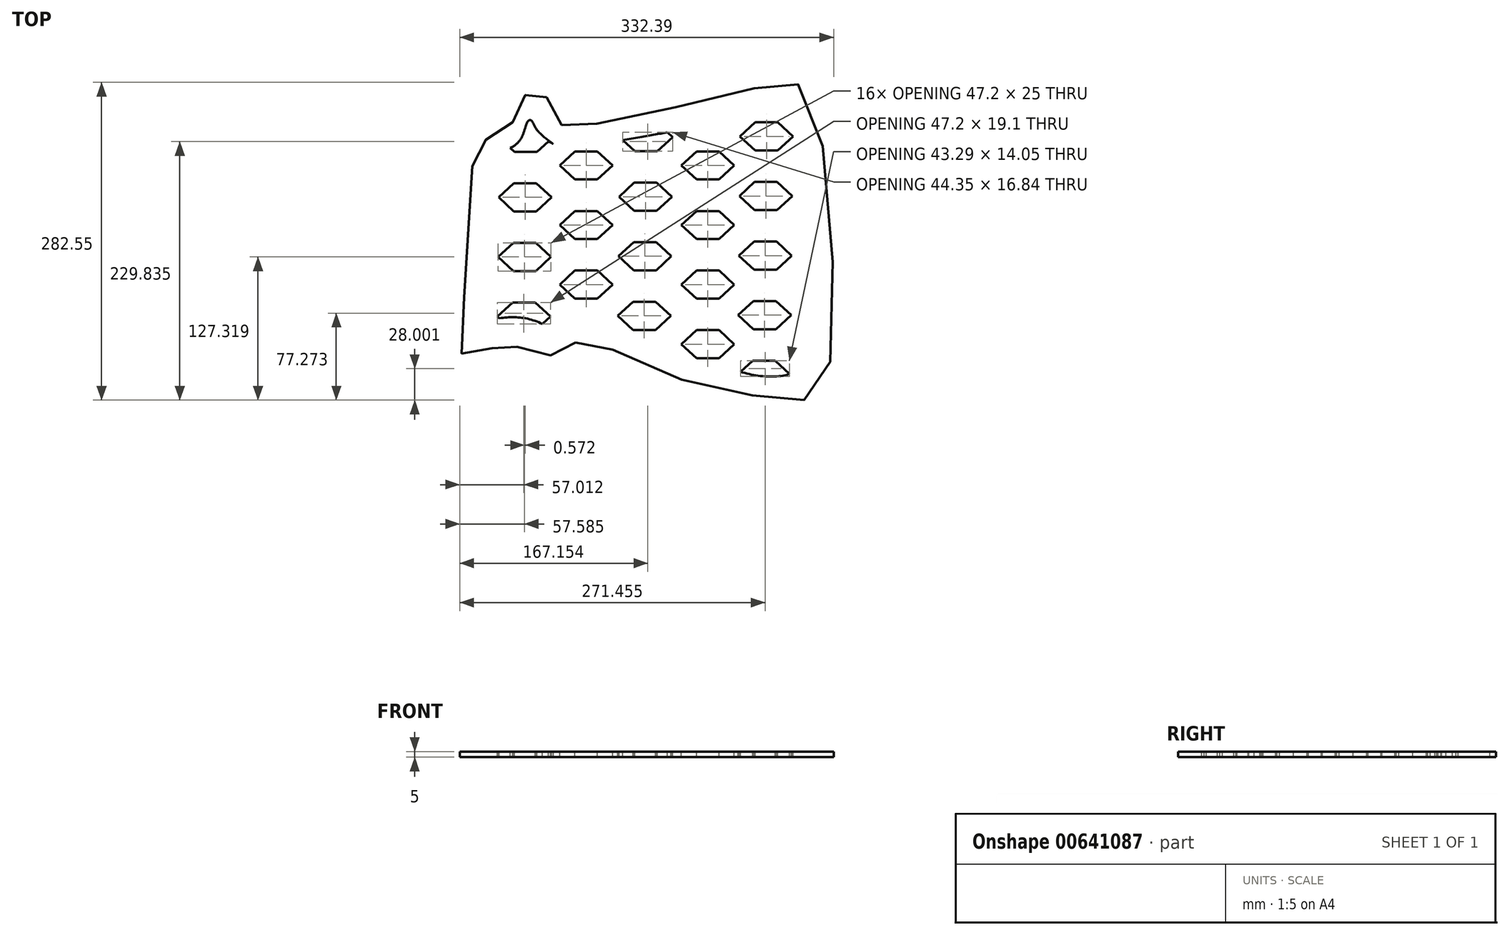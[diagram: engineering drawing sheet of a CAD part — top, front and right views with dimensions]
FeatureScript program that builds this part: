
annotation { "Feature Type Name" : "Feature", "Feature Type Description" : "" }
export const myFeature = defineFeature(function(context is Context, id is Id, definition is map)
    precondition{}
    {
        {
            var Q0;
            Q0=qCreatedBy(makeId("Top.planeOp"),FACE);
            var sketch = newSketch(context, id + "F0", { "sketchPlane" : qUnion([Q0])});
            skFitSpline(sketch, "E0", {"points": [v(-94.07, -91.9) * mm, v(-73.28, -91.9) * mm, v(-51.22, -104.21) * mm, v(37.87, -135.18) * mm, v(78.6, -140.27) * mm, v(113.8, -141.97) * mm, v(129.5, -122.03) * mm, v(133.1, 8.11) * mm, v(111.47, 130.93) * mm, v(94.35, 139.49) * mm, v(62.95, 133.78) * mm, v(-26.95, 112.38) * mm, v(-91.16, 100.96) * mm, v(-103.99, 100.98) * mm, v(-106.66, 101.88) * mm, v(-111.48, 110.97) * mm, v(-119.2, 125.34) * mm, v(-130.98, 133.72) * mm, v(-136.33, 132.65) * mm, v(-140.08, 124.45) * mm, v(-144.54, 111.78) * mm, v(-151.14, 102.68) * mm, v(-161.84, 93.4) * mm, v(-175.4, 88.06) * mm, v(-183.06, 84.5) * mm, v(-185.2, 75.21) * mm, v(-196.64, -95.2) * mm, v(-196.85, -99.64) * mm, v(-194.63, -102.29) * mm, v(-190.38, -103.77) * mm, v(-170.02, -97.51) * mm, v(-163.87, -94.97) * mm, v(-157.5, -91.79) * mm, v(-139.47, -99) * mm, v(-122.77, -103.85) * mm, v(-112.2, -101.6) * mm, v(-101.44, -94.98) * mm, v(-94.07, -91.9) * mm]});
            skSolve(sketch);
        }
        {
            var Q0;
            Q0 = qSketchRegion(id + "F0", true);
            extrude(context, id + "F1", {"entities" : qUnion([Q0]), "depth" : 5 * mm, "offsetDistance" : 25.4 * mm});
        }
        {
            var Q0;
            Q0=makeQuery(id+"F1.opExtrude","CAP_FACE",FACE,{"disambiguationData":[OSD([sQuery(id+"F0.wireOp",EDGE,"E0")])],"isStart":false});
            var sketch = newSketch(context, id + "F2", { "sketchPlane" : qUnion([Q0])});
            skLineSegment(sketch, "E1.bottom", {"start": v(65.65, 103.96) * mm, "end": v(85.65, 103.96) * mm});
            skLineSegment(sketch, "E1.top", {"start": v(65.65, 78.96) * mm, "end": v(85.65, 78.96) * mm});
            skLineSegment(sketch, "E2", {"start": v(65.65, 103.96) * mm, "end": v(52.05, 91.46) * mm});
            skPoint(sketch, "E2.endSnap0", {"position": v(65.65, 91.46) * mm});
            skLineSegment(sketch, "E3", {"start": v(52.05, 91.46) * mm, "end": v(65.65, 78.96) * mm});
            skLineSegment(sketch, "E4.MirrorCS", {"start": v(85.65, 103.96) * mm, "end": v(99.24, 91.46) * mm});
            skLineSegment(sketch, "E5.MirrorCS", {"start": v(99.24, 91.46) * mm, "end": v(85.65, 78.96) * mm});
            skLineSegment(sketch, "E6.0.1.0", {"start": v(-52.1, 88.23) * mm, "end": v(-41.35, 78.35) * mm});
            skLineSegment(sketch, "E6.0.1.1", {"start": v(-41.35, 103.35) * mm, "end": v(-54.95, 90.85) * mm});
            skLineSegment(sketch, "E6.0.1.2", {"start": v(-41.35, 103.35) * mm, "end": v(-21.35, 103.35) * mm});
            skLineSegment(sketch, "E6.0.1.3", {"start": v(-12.48, 95.2) * mm, "end": v(-7.75, 90.85) * mm});
            skLineSegment(sketch, "E6.0.1.4", {"start": v(-7.75, 90.85) * mm, "end": v(-21.35, 78.35) * mm});
            skLineSegment(sketch, "E6.0.1.5", {"start": v(-41.35, 78.35) * mm, "end": v(-21.35, 78.35) * mm});
            skLineSegment(sketch, "E6.1.0.0", {"start": v(51.47, 38.46) * mm, "end": v(65.07, 25.96) * mm});
            skLineSegment(sketch, "E6.1.0.1", {"start": v(65.07, 50.96) * mm, "end": v(51.47, 38.46) * mm});
            skLineSegment(sketch, "E6.1.0.2", {"start": v(65.07, 50.96) * mm, "end": v(85.07, 50.96) * mm});
            skLineSegment(sketch, "E6.1.0.3", {"start": v(85.07, 50.96) * mm, "end": v(98.67, 38.46) * mm});
            skLineSegment(sketch, "E6.1.0.4", {"start": v(98.67, 38.46) * mm, "end": v(85.07, 25.96) * mm});
            skLineSegment(sketch, "E6.1.0.5", {"start": v(65.07, 25.96) * mm, "end": v(85.07, 25.96) * mm});
            skLineSegment(sketch, "E6.1.1.0", {"start": v(-55.52, 37.86) * mm, "end": v(-41.92, 25.36) * mm});
            skLineSegment(sketch, "E6.1.1.1", {"start": v(-41.92, 50.36) * mm, "end": v(-55.52, 37.86) * mm});
            skLineSegment(sketch, "E6.1.1.2", {"start": v(-41.92, 50.36) * mm, "end": v(-21.92, 50.36) * mm});
            skLineSegment(sketch, "E6.1.1.3", {"start": v(-21.92, 50.36) * mm, "end": v(-8.33, 37.86) * mm});
            skLineSegment(sketch, "E6.1.1.4", {"start": v(-8.33, 37.86) * mm, "end": v(-21.92, 25.36) * mm});
            skLineSegment(sketch, "E6.1.1.5", {"start": v(-41.92, 25.36) * mm, "end": v(-21.92, 25.36) * mm});
            skLineSegment(sketch, "E6.2.0.0", {"start": v(50.9, -14.54) * mm, "end": v(64.5, -27.04) * mm});
            skLineSegment(sketch, "E6.2.0.1", {"start": v(64.5, -2.04) * mm, "end": v(50.9, -14.54) * mm});
            skLineSegment(sketch, "E6.2.0.2", {"start": v(64.5, -2.04) * mm, "end": v(84.5, -2.04) * mm});
            skLineSegment(sketch, "E6.2.0.3", {"start": v(84.5, -2.04) * mm, "end": v(98.1, -14.54) * mm});
            skLineSegment(sketch, "E6.2.0.4", {"start": v(98.1, -14.54) * mm, "end": v(84.5, -27.04) * mm});
            skLineSegment(sketch, "E6.2.0.5", {"start": v(64.5, -27.04) * mm, "end": v(84.5, -27.04) * mm});
            skLineSegment(sketch, "E6.2.1.0", {"start": v(-56.1, -15.14) * mm, "end": v(-42.5, -27.64) * mm});
            skLineSegment(sketch, "E6.2.1.1", {"start": v(-42.5, -2.64) * mm, "end": v(-56.1, -15.14) * mm});
            skLineSegment(sketch, "E6.2.1.2", {"start": v(-42.5, -2.64) * mm, "end": v(-22.5, -2.64) * mm});
            skLineSegment(sketch, "E6.2.1.3", {"start": v(-22.5, -2.64) * mm, "end": v(-8.9, -15.14) * mm});
            skLineSegment(sketch, "E6.2.1.4", {"start": v(-8.9, -15.14) * mm, "end": v(-22.5, -27.64) * mm});
            skLineSegment(sketch, "E6.2.1.5", {"start": v(-42.5, -27.64) * mm, "end": v(-22.5, -27.64) * mm});
            skLineSegment(sketch, "E6.direction1", {"start": v(52.05, 91.46) * mm, "end": v(51.47, 38.46) * mm, "construction": true});
            skLineSegment(sketch, "E6.direction2", {"start": v(52.05, 91.46) * mm, "end": v(-54.95, 90.85) * mm, "construction": true});
            skLineSegment(sketch, "E7.0.0.2", {"start": v(-152.06, 81.16) * mm, "end": v(-148.35, 77.75) * mm});
            skLineSegment(sketch, "E7.3.0.2", {"start": v(-148.35, 102.75) * mm, "end": v(-161.95, 90.25) * mm});
            skLineSegment(sketch, "E7.6.0.2", {"start": v(-148.35, 102.75) * mm, "end": v(-128.35, 102.75) * mm});
            skLineSegment(sketch, "E7.9.0.2", {"start": v(-128.35, 102.75) * mm, "end": v(-114.75, 90.25) * mm});
            skLineSegment(sketch, "E7.12.0.2", {"start": v(-117.71, 87.53) * mm, "end": v(-128.35, 77.75) * mm});
            skLineSegment(sketch, "E7.15.0.2", {"start": v(-148.35, 77.75) * mm, "end": v(-128.35, 77.75) * mm});
            skLineSegment(sketch, "E7.0.1.2", {"start": v(-162.52, 37.26) * mm, "end": v(-148.92, 24.76) * mm});
            skLineSegment(sketch, "E7.3.1.2", {"start": v(-148.92, 49.76) * mm, "end": v(-162.52, 37.26) * mm});
            skLineSegment(sketch, "E7.6.1.2", {"start": v(-148.92, 49.76) * mm, "end": v(-128.92, 49.76) * mm});
            skLineSegment(sketch, "E7.9.1.2", {"start": v(-128.92, 49.76) * mm, "end": v(-115.32, 37.26) * mm});
            skLineSegment(sketch, "E7.12.1.2", {"start": v(-115.32, 37.26) * mm, "end": v(-128.92, 24.76) * mm});
            skLineSegment(sketch, "E7.15.1.2", {"start": v(-148.92, 24.76) * mm, "end": v(-128.92, 24.76) * mm});
            skLineSegment(sketch, "E7.0.2.2", {"start": v(-163.1, -15.74) * mm, "end": v(-149.5, -28.24) * mm});
            skLineSegment(sketch, "E7.3.2.2", {"start": v(-149.5, -3.24) * mm, "end": v(-163.1, -15.74) * mm});
            skLineSegment(sketch, "E7.6.2.2", {"start": v(-149.5, -3.24) * mm, "end": v(-129.5, -3.24) * mm});
            skLineSegment(sketch, "E7.9.2.2", {"start": v(-129.5, -3.24) * mm, "end": v(-115.9, -15.74) * mm});
            skLineSegment(sketch, "E7.12.2.2", {"start": v(-115.9, -15.74) * mm, "end": v(-129.5, -28.24) * mm});
            skLineSegment(sketch, "E7.15.2.2", {"start": v(-149.5, -28.24) * mm, "end": v(-129.5, -28.24) * mm});
            skLineSegment(sketch, "E8.0.3.0", {"start": v(50.33, -67.54) * mm, "end": v(63.93, -80.04) * mm});
            skLineSegment(sketch, "E8.3.3.0", {"start": v(63.93, -55.04) * mm, "end": v(50.33, -67.54) * mm});
            skLineSegment(sketch, "E8.6.3.0", {"start": v(63.93, -55.04) * mm, "end": v(83.93, -55.04) * mm});
            skLineSegment(sketch, "E8.9.3.0", {"start": v(83.93, -55.04) * mm, "end": v(97.53, -67.54) * mm});
            skLineSegment(sketch, "E8.12.3.0", {"start": v(97.53, -67.54) * mm, "end": v(83.93, -80.04) * mm});
            skLineSegment(sketch, "E8.15.3.0", {"start": v(63.93, -80.04) * mm, "end": v(83.93, -80.04) * mm});
            skLineSegment(sketch, "E8.0.3.1", {"start": v(-56.67, -68.14) * mm, "end": v(-43.07, -80.64) * mm});
            skLineSegment(sketch, "E8.3.3.1", {"start": v(-43.07, -55.64) * mm, "end": v(-56.67, -68.14) * mm});
            skLineSegment(sketch, "E8.6.3.1", {"start": v(-43.07, -55.64) * mm, "end": v(-23.07, -55.64) * mm});
            skLineSegment(sketch, "E8.9.3.1", {"start": v(-23.07, -55.64) * mm, "end": v(-9.47, -68.14) * mm});
            skLineSegment(sketch, "E8.12.3.1", {"start": v(-9.47, -68.14) * mm, "end": v(-23.07, -80.64) * mm});
            skLineSegment(sketch, "E8.15.3.1", {"start": v(-43.07, -80.64) * mm, "end": v(-23.07, -80.64) * mm});
            skLineSegment(sketch, "E8.0.3.2", {"start": v(-163.67, -68.74) * mm, "end": v(-161.99, -70.28) * mm});
            skLineSegment(sketch, "E8.3.3.2", {"start": v(-150.07, -56.24) * mm, "end": v(-163.67, -68.74) * mm});
            skLineSegment(sketch, "E8.6.3.2", {"start": v(-150.07, -56.24) * mm, "end": v(-130.07, -56.24) * mm});
            skLineSegment(sketch, "E8.9.3.2", {"start": v(-130.07, -56.24) * mm, "end": v(-116.47, -68.74) * mm});
            skLineSegment(sketch, "E8.12.3.2", {"start": v(-116.47, -68.74) * mm, "end": v(-123.65, -75.34) * mm});
            skLineSegment(sketch, "E8.15.3.2", {"start": v(-150.07, -81.24) * mm, "end": v(-130.07, -81.24) * mm});
            skLineSegment(sketch, "E9.3.4.0", {"start": v(63.36, -108.03) * mm, "end": v(49.76, -120.53) * mm});
            skLineSegment(sketch, "E9.6.4.0", {"start": v(63.36, -108.03) * mm, "end": v(83.36, -108.03) * mm});
            skLineSegment(sketch, "E9.9.4.0", {"start": v(83.36, -108.03) * mm, "end": v(96.96, -120.53) * mm});
            skLineSegment(sketch, "E9.12.4.0", {"start": v(96.96, -120.53) * mm, "end": v(89.16, -127.7) * mm});
            skLineSegment(sketch, "E9.15.4.0", {"start": v(63.36, -133.03) * mm, "end": v(83.36, -133.03) * mm});
            skLineSegment(sketch, "E9.0.4.1", {"start": v(-57.24, -121.13) * mm, "end": v(-43.64, -133.63) * mm});
            skLineSegment(sketch, "E9.3.4.1", {"start": v(-43.64, -108.63) * mm, "end": v(-57.24, -121.13) * mm});
            skLineSegment(sketch, "E9.9.4.1", {"start": v(-23.64, -108.63) * mm, "end": v(-10.04, -121.13) * mm});
            skLineSegment(sketch, "E9.12.4.1", {"start": v(-10.04, -121.13) * mm, "end": v(-23.64, -133.63) * mm});
            skLineSegment(sketch, "E9.15.4.1", {"start": v(-43.64, -133.63) * mm, "end": v(-23.64, -133.63) * mm});
            skLineSegment(sketch, "E9.0.4.2", {"start": v(-164.24, -121.73) * mm, "end": v(-150.64, -134.23) * mm});
            skLineSegment(sketch, "E9.3.4.2", {"start": v(-150.64, -109.23) * mm, "end": v(-164.24, -121.73) * mm});
            skLineSegment(sketch, "E9.6.4.2", {"start": v(-150.64, -109.23) * mm, "end": v(-130.64, -109.23) * mm});
            skLineSegment(sketch, "E9.12.4.2", {"start": v(-117.04, -121.73) * mm, "end": v(-130.64, -134.23) * mm});
            skLineSegment(sketch, "E9.15.4.2", {"start": v(-150.64, -134.23) * mm, "end": v(-130.64, -134.23) * mm});
            skPoint(sketch, "E10.5.internal.snap0", {"position": v(-121.55, 84) * mm});
            skFitSpline(sketch, "E10", {"points": [v(-161.35, 77.3) * mm, v(-143.19, 88.6) * mm, v(-136.33, 105.15) * mm, v(-133.5, 105.76) * mm, v(-129.47, 98.7) * mm, v(-112.92, 84) * mm], "startDerivative": vector(83.4, 30.91) * mm, "endDerivative": vector(77, -56.15) * mm});
            skFitSpline(sketch, "E11.trimOffspring", {"points": [v(-161.35, 77.3) * mm, v(-143.19, 88.6) * mm, v(-136.33, 105.15) * mm, v(-133.5, 105.76) * mm, v(-129.47, 98.7) * mm, v(-112.92, 84) * mm], "startDerivative": vector(83.4, 30.91) * mm, "endDerivative": vector(77, -56.15) * mm});
            skFitSpline(sketch, "E12", {"points": [v(-65.4, 86.04) * mm, v(0, 97.95) * mm, v(10.07, 101.38) * mm], "startDerivative": vector(111.67, 18.33) * mm, "endDerivative": vector(27.2, 11.34) * mm});
            skPoint(sketch, "E13.orphan", {"position": v(-21.35, 103.35) * mm});
            skPoint(sketch, "E14.1.internal.snap0", {"position": v(90.16, -126.78) * mm});
            skPoint(sketch, "E15.orphan", {"position": v(83.36, -133.03) * mm});
            skFitSpline(sketch, "E16", {"points": [v(-149.57, 84.61) * mm, v(-135.6, 92.03) * mm, v(-109.34, 82.33) * mm], "startDerivative": vector(29.7, 24.64) * mm, "endDerivative": vector(49.83, -26.78) * mm});
            skPoint(sketch, "E17.2.internal.snap0", {"position": v(-123.27, -74.99) * mm});
            skFitSpline(sketch, "E17", {"points": [v(-88.58, -98.82) * mm, v(-137.18, -70.57) * mm, v(-184.13, -74.99) * mm], "startDerivative": vector(-91.79, 70.65) * mm, "endDerivative": vector(-99.41, -24.39) * mm});
            skPoint(sketch, "E18.orphan", {"position": v(-130.07, -81.24) * mm});
            skFitSpline(sketch, "E19", {"points": [v(38.58, -112.96) * mm, v(73.26, -121.9) * mm, v(98.5, -118.05) * mm, v(98.92, -112.86) * mm], "startDerivative": vector(73.84, -26.66) * mm, "endDerivative": vector(-8, 32.55) * mm});
            skSolve(sketch);
        }
        {
            var Q0;
            Q0=makeQuery(id+"F2.imprint","IMPRINT",FACE,{"disambiguationData":[TD([[makeQuery(id+"F2.imprint","IMPRINT",EDGE,{"derivedFrom":sQuery(id+"F2.wireOp",EDGE,"E1.bottom")}),1.0]])]});
            var sketch = newSketch(context, id + "F3", { "sketchPlane" : qUnion([Q0])});
            skLineSegment(sketch, "E20.bottom", {"start": v(13.37, 78.17) * mm, "end": v(33.37, 78.17) * mm});
            skLineSegment(sketch, "E20.top", {"start": v(13.37, 53.17) * mm, "end": v(33.37, 53.17) * mm});
            skLineSegment(sketch, "E21", {"start": v(13.37, 78.17) * mm, "end": v(-0.23, 65.67) * mm});
            skPoint(sketch, "E21.endSnap0", {"position": v(13.37, 65.67) * mm});
            skLineSegment(sketch, "E22", {"start": v(-0.23, 65.67) * mm, "end": v(13.37, 53.17) * mm});
            skLineSegment(sketch, "E23.MirrorCS", {"start": v(33.37, 78.17) * mm, "end": v(46.97, 65.67) * mm});
            skLineSegment(sketch, "E24.MirrorCS", {"start": v(46.97, 65.67) * mm, "end": v(33.37, 53.17) * mm});
            skLineSegment(sketch, "E25.direction1", {"start": v(-0.23, 65.67) * mm, "end": v(-0.8, 12.67) * mm, "construction": true});
            skLineSegment(sketch, "E25.direction2", {"start": v(-0.23, 65.67) * mm, "end": v(-107.22, 65.07) * mm, "construction": true});
            skPoint(sketch, "E26.0.1.0", {"position": v(13.37, 12.67) * mm});
            skLineSegment(sketch, "E26.0.1.1", {"start": v(-0.23, 12.67) * mm, "end": v(-0.8, -40.33) * mm, "construction": true});
            skLineSegment(sketch, "E26.0.1.2", {"start": v(46.97, 12.67) * mm, "end": v(33.37, 0.17) * mm});
            skLineSegment(sketch, "E26.0.1.3", {"start": v(33.37, 25.17) * mm, "end": v(46.97, 12.67) * mm});
            skLineSegment(sketch, "E26.0.1.4", {"start": v(-0.23, 12.67) * mm, "end": v(13.37, 0.17) * mm});
            skLineSegment(sketch, "E26.0.1.5", {"start": v(13.37, 25.17) * mm, "end": v(-0.23, 12.67) * mm});
            skLineSegment(sketch, "E26.0.1.6", {"start": v(13.37, 0.17) * mm, "end": v(33.37, 0.17) * mm});
            skLineSegment(sketch, "E26.0.1.7", {"start": v(13.37, 25.17) * mm, "end": v(33.37, 25.17) * mm});
            skLineSegment(sketch, "E26.0.1.8", {"start": v(-0.23, 12.67) * mm, "end": v(-107.22, 12.07) * mm, "construction": true});
            skPoint(sketch, "E26.0.2.0", {"position": v(13.37, -40.33) * mm});
            skLineSegment(sketch, "E26.0.2.1", {"start": v(-0.23, -40.33) * mm, "end": v(-0.8, -93.33) * mm, "construction": true});
            skLineSegment(sketch, "E26.0.2.2", {"start": v(46.97, -40.33) * mm, "end": v(33.37, -52.83) * mm});
            skLineSegment(sketch, "E26.0.2.3", {"start": v(33.37, -27.83) * mm, "end": v(46.97, -40.33) * mm});
            skLineSegment(sketch, "E26.0.2.4", {"start": v(-0.23, -40.33) * mm, "end": v(13.37, -52.83) * mm});
            skLineSegment(sketch, "E26.0.2.5", {"start": v(13.37, -27.83) * mm, "end": v(-0.23, -40.33) * mm});
            skLineSegment(sketch, "E26.0.2.6", {"start": v(13.37, -52.83) * mm, "end": v(33.37, -52.83) * mm});
            skLineSegment(sketch, "E26.0.2.7", {"start": v(13.37, -27.83) * mm, "end": v(33.37, -27.83) * mm});
            skLineSegment(sketch, "E26.0.2.8", {"start": v(-0.23, -40.33) * mm, "end": v(-107.22, -40.93) * mm, "construction": true});
            skPoint(sketch, "E26.0.3.0", {"position": v(13.37, -93.33) * mm});
            skLineSegment(sketch, "E26.0.3.1", {"start": v(-0.23, -93.33) * mm, "end": v(-0.8, -146.33) * mm, "construction": true});
            skLineSegment(sketch, "E26.0.3.2", {"start": v(46.97, -93.33) * mm, "end": v(33.37, -105.83) * mm});
            skLineSegment(sketch, "E26.0.3.3", {"start": v(33.37, -80.83) * mm, "end": v(46.97, -93.33) * mm});
            skLineSegment(sketch, "E26.0.3.4", {"start": v(-0.23, -93.33) * mm, "end": v(13.37, -105.83) * mm});
            skLineSegment(sketch, "E26.0.3.5", {"start": v(13.37, -80.83) * mm, "end": v(-0.23, -93.33) * mm});
            skLineSegment(sketch, "E26.0.3.6", {"start": v(13.37, -105.83) * mm, "end": v(33.37, -105.83) * mm});
            skLineSegment(sketch, "E26.0.3.7", {"start": v(13.37, -80.83) * mm, "end": v(33.37, -80.83) * mm});
            skLineSegment(sketch, "E26.0.3.8", {"start": v(-0.23, -93.33) * mm, "end": v(-107.22, -93.93) * mm, "construction": true});
            skPoint(sketch, "E26.1.0.0", {"position": v(-94.63, 65.67) * mm});
            skLineSegment(sketch, "E26.1.0.1", {"start": v(-108.23, 65.67) * mm, "end": v(-108.8, 12.67) * mm, "construction": true});
            skLineSegment(sketch, "E26.1.0.2", {"start": v(-61.03, 65.67) * mm, "end": v(-74.63, 53.17) * mm});
            skLineSegment(sketch, "E26.1.0.3", {"start": v(-74.63, 78.17) * mm, "end": v(-61.03, 65.67) * mm});
            skLineSegment(sketch, "E26.1.0.4", {"start": v(-108.23, 65.67) * mm, "end": v(-94.63, 53.17) * mm});
            skLineSegment(sketch, "E26.1.0.5", {"start": v(-94.63, 78.17) * mm, "end": v(-108.23, 65.67) * mm});
            skLineSegment(sketch, "E26.1.0.6", {"start": v(-94.63, 53.17) * mm, "end": v(-74.63, 53.17) * mm});
            skLineSegment(sketch, "E26.1.0.7", {"start": v(-94.63, 78.17) * mm, "end": v(-74.63, 78.17) * mm});
            skLineSegment(sketch, "E26.1.0.8", {"start": v(-108.23, 65.67) * mm, "end": v(-215.22, 65.07) * mm, "construction": true});
            skPoint(sketch, "E26.1.1.0", {"position": v(-94.63, 12.67) * mm});
            skLineSegment(sketch, "E26.1.1.1", {"start": v(-108.23, 12.67) * mm, "end": v(-108.8, -40.33) * mm, "construction": true});
            skLineSegment(sketch, "E26.1.1.2", {"start": v(-61.03, 12.67) * mm, "end": v(-74.63, 0.17) * mm});
            skLineSegment(sketch, "E26.1.1.3", {"start": v(-74.63, 25.17) * mm, "end": v(-61.03, 12.67) * mm});
            skLineSegment(sketch, "E26.1.1.4", {"start": v(-108.23, 12.67) * mm, "end": v(-94.63, 0.17) * mm});
            skLineSegment(sketch, "E26.1.1.5", {"start": v(-94.63, 25.17) * mm, "end": v(-108.23, 12.67) * mm});
            skLineSegment(sketch, "E26.1.1.6", {"start": v(-94.63, 0.17) * mm, "end": v(-74.63, 0.17) * mm});
            skLineSegment(sketch, "E26.1.1.7", {"start": v(-94.63, 25.17) * mm, "end": v(-74.63, 25.17) * mm});
            skLineSegment(sketch, "E26.1.1.8", {"start": v(-108.23, 12.67) * mm, "end": v(-215.22, 12.07) * mm, "construction": true});
            skPoint(sketch, "E26.1.2.0", {"position": v(-94.63, -40.33) * mm});
            skLineSegment(sketch, "E26.1.2.1", {"start": v(-108.23, -40.33) * mm, "end": v(-108.8, -93.33) * mm, "construction": true});
            skLineSegment(sketch, "E26.1.2.2", {"start": v(-61.03, -40.33) * mm, "end": v(-74.63, -52.83) * mm});
            skLineSegment(sketch, "E26.1.2.3", {"start": v(-74.63, -27.83) * mm, "end": v(-61.03, -40.33) * mm});
            skLineSegment(sketch, "E26.1.2.4", {"start": v(-108.23, -40.33) * mm, "end": v(-94.63, -52.83) * mm});
            skLineSegment(sketch, "E26.1.2.5", {"start": v(-94.63, -27.83) * mm, "end": v(-108.23, -40.33) * mm});
            skLineSegment(sketch, "E26.1.2.6", {"start": v(-94.63, -52.83) * mm, "end": v(-74.63, -52.83) * mm});
            skLineSegment(sketch, "E26.1.2.7", {"start": v(-94.63, -27.83) * mm, "end": v(-74.63, -27.83) * mm});
            skLineSegment(sketch, "E26.1.2.8", {"start": v(-108.23, -40.33) * mm, "end": v(-215.22, -40.93) * mm, "construction": true});
            skPoint(sketch, "E26.1.3.0", {"position": v(-94.63, -93.33) * mm});
            skLineSegment(sketch, "E26.1.3.1", {"start": v(-108.23, -93.33) * mm, "end": v(-108.8, -146.33) * mm, "construction": true});
            skLineSegment(sketch, "E26.1.3.2", {"start": v(-61.03, -93.33) * mm, "end": v(-74.63, -105.83) * mm});
            skLineSegment(sketch, "E26.1.3.3", {"start": v(-74.63, -80.83) * mm, "end": v(-61.03, -93.33) * mm});
            skLineSegment(sketch, "E26.1.3.4", {"start": v(-108.23, -93.33) * mm, "end": v(-94.63, -105.83) * mm});
            skLineSegment(sketch, "E26.1.3.6", {"start": v(-94.63, -105.83) * mm, "end": v(-74.63, -105.83) * mm});
            skLineSegment(sketch, "E26.1.3.7", {"start": v(-94.63, -80.83) * mm, "end": v(-74.63, -80.83) * mm});
            skLineSegment(sketch, "E26.1.3.8", {"start": v(-108.23, -93.33) * mm, "end": v(-215.22, -93.93) * mm, "construction": true});
            skPoint(sketch, "E26.2.0.0", {"position": v(-202.63, 65.67) * mm});
            skLineSegment(sketch, "E26.2.0.1", {"start": v(-216.23, 65.67) * mm, "end": v(-216.8, 12.67) * mm, "construction": true});
            skLineSegment(sketch, "E26.2.0.2", {"start": v(-169.03, 65.67) * mm, "end": v(-169.68, 65.07) * mm});
            skLineSegment(sketch, "E26.2.0.3", {"start": v(-182.63, 78.17) * mm, "end": v(-169.03, 65.67) * mm});
            skLineSegment(sketch, "E26.2.0.4", {"start": v(-216.23, 65.67) * mm, "end": v(-202.63, 53.17) * mm});
            skLineSegment(sketch, "E26.2.0.5", {"start": v(-202.63, 78.17) * mm, "end": v(-216.23, 65.67) * mm});
            skLineSegment(sketch, "E26.2.0.6", {"start": v(-202.63, 53.17) * mm, "end": v(-182.63, 53.17) * mm});
            skLineSegment(sketch, "E26.2.0.7", {"start": v(-202.63, 78.17) * mm, "end": v(-182.63, 78.17) * mm});
            skLineSegment(sketch, "E26.2.0.8", {"start": v(-216.23, 65.67) * mm, "end": v(-323.22, 65.07) * mm, "construction": true});
            skPoint(sketch, "E26.2.1.0", {"position": v(-202.63, 12.67) * mm});
            skLineSegment(sketch, "E26.2.1.1", {"start": v(-216.23, 12.67) * mm, "end": v(-216.8, -40.33) * mm, "construction": true});
            skLineSegment(sketch, "E26.2.1.2", {"start": v(-169.03, 12.67) * mm, "end": v(-169.4, 12.33) * mm});
            skLineSegment(sketch, "E26.2.1.3", {"start": v(-182.63, 25.17) * mm, "end": v(-169.03, 12.67) * mm});
            skLineSegment(sketch, "E26.2.1.4", {"start": v(-216.23, 12.67) * mm, "end": v(-202.63, 0.17) * mm});
            skLineSegment(sketch, "E26.2.1.5", {"start": v(-202.63, 25.17) * mm, "end": v(-216.23, 12.67) * mm});
            skLineSegment(sketch, "E26.2.1.6", {"start": v(-202.63, 0.17) * mm, "end": v(-182.63, 0.17) * mm});
            skLineSegment(sketch, "E26.2.1.7", {"start": v(-202.63, 25.17) * mm, "end": v(-182.63, 25.17) * mm});
            skLineSegment(sketch, "E26.2.1.8", {"start": v(-216.23, 12.67) * mm, "end": v(-323.22, 12.07) * mm, "construction": true});
            skPoint(sketch, "E26.2.2.0", {"position": v(-202.63, -40.33) * mm});
            skLineSegment(sketch, "E26.2.2.1", {"start": v(-216.23, -40.33) * mm, "end": v(-216.8, -93.33) * mm, "construction": true});
            skLineSegment(sketch, "E26.2.2.2", {"start": v(-169.03, -40.33) * mm, "end": v(-169.4, -40.67) * mm});
            skLineSegment(sketch, "E26.2.2.3", {"start": v(-182.63, -27.83) * mm, "end": v(-169.03, -40.33) * mm});
            skLineSegment(sketch, "E26.2.2.4", {"start": v(-216.23, -40.33) * mm, "end": v(-202.63, -52.83) * mm});
            skLineSegment(sketch, "E26.2.2.5", {"start": v(-202.63, -27.83) * mm, "end": v(-216.23, -40.33) * mm});
            skLineSegment(sketch, "E26.2.2.6", {"start": v(-202.63, -52.83) * mm, "end": v(-182.63, -52.83) * mm});
            skLineSegment(sketch, "E26.2.2.7", {"start": v(-202.63, -27.83) * mm, "end": v(-182.63, -27.83) * mm});
            skLineSegment(sketch, "E26.2.2.8", {"start": v(-216.23, -40.33) * mm, "end": v(-323.22, -40.93) * mm, "construction": true});
            skPoint(sketch, "E26.2.3.0", {"position": v(-202.63, -93.33) * mm});
            skLineSegment(sketch, "E26.2.3.1", {"start": v(-216.23, -93.33) * mm, "end": v(-216.8, -146.33) * mm, "construction": true});
            skLineSegment(sketch, "E26.2.3.2", {"start": v(-169.03, -93.33) * mm, "end": v(-182.63, -105.83) * mm});
            skLineSegment(sketch, "E26.2.3.4", {"start": v(-216.23, -93.33) * mm, "end": v(-202.63, -105.83) * mm});
            skLineSegment(sketch, "E26.2.3.5", {"start": v(-202.63, -80.83) * mm, "end": v(-216.23, -93.33) * mm});
            skLineSegment(sketch, "E26.2.3.6", {"start": v(-202.63, -105.83) * mm, "end": v(-182.63, -105.83) * mm});
            skLineSegment(sketch, "E26.2.3.7", {"start": v(-202.63, -80.83) * mm, "end": v(-182.63, -80.83) * mm});
            skLineSegment(sketch, "E26.2.3.8", {"start": v(-216.23, -93.33) * mm, "end": v(-323.22, -93.93) * mm, "construction": true});
            skLineSegment(sketch, "E26.direction1", {"start": v(-107.22, 65.07) * mm, "end": v(-215.22, 65.07) * mm, "construction": true});
            skLineSegment(sketch, "E26.direction2", {"start": v(-107.22, 65.07) * mm, "end": v(-107.22, 12.07) * mm, "construction": true});
            skPoint(sketch, "E27.orphan", {"position": v(-182.63, -52.83) * mm});
            skPoint(sketch, "E28.orphan", {"position": v(-182.63, 0.17) * mm});
            skPoint(sketch, "E29.orphan", {"position": v(-182.63, 53.17) * mm});
            skSolve(sketch);
        }
        {
            var Q0;
            Q0 = qSketchRegion(id + "F2", true);
            extrude(context, id + "F4", {"entities" : qUnion([Q0]), "operationType" : NewBodyOperationType.REMOVE, "oppositeDirection" : true, "depth" : 25 * mm, "offsetDistance" : 25 * mm});
        }
        {
            var Q0;
            Q0 = qSketchRegion(id + "F3", true);
            extrude(context, id + "F5", {"entities" : qUnion([Q0]), "operationType" : NewBodyOperationType.REMOVE, "oppositeDirection" : true, "depth" : 25 * mm, "offsetDistance" : 25 * mm});
        }
    });
